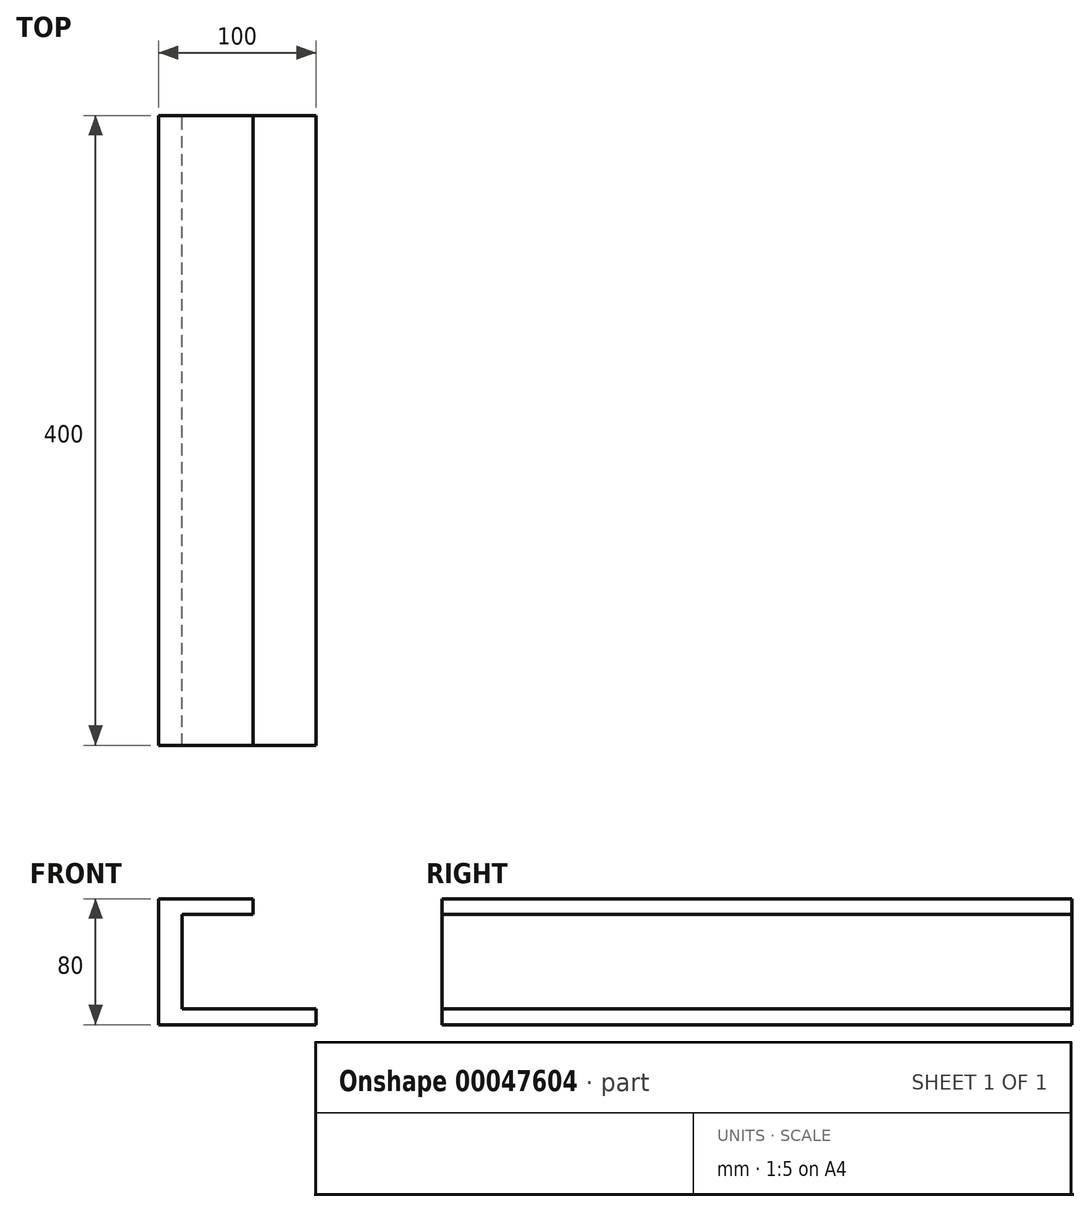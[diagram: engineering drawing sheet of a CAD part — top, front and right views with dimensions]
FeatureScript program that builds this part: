
annotation { "Feature Type Name" : "Feature", "Feature Type Description" : "" }
export const myFeature = defineFeature(function(context is Context, id is Id, definition is map)
    precondition{}
    {
        {
            var Q0;
            Q0=qCreatedBy(makeId("Front.planeOp"),FACE);
            var sketch = newSketch(context, id + "F0", { "sketchPlane" : qUnion([Q0])});
            skLineSegment(sketch, "E0.bottom", {"start": v(0, 0) * mm, "end": v(100, 0) * mm});
            skLineSegment(sketch, "E0.top", {"start": v(15, 10) * mm, "end": v(100, 10) * mm});
            skLineSegment(sketch, "E0.right", {"start": v(100, 0) * mm, "end": v(100, 10) * mm});
            skLineSegment(sketch, "E1", {"start": v(15, 10) * mm, "end": v(15, 70) * mm});
            skLineSegment(sketch, "E2", {"start": v(15, 70) * mm, "end": v(60, 70) * mm});
            skLineSegment(sketch, "E3", {"start": v(60, 70) * mm, "end": v(60, 80) * mm});
            skLineSegment(sketch, "E4", {"start": v(60, 80) * mm, "end": v(0, 80) * mm});
            skLineSegment(sketch, "E5", {"start": v(0, 80) * mm, "end": v(0, 0) * mm});
            skSolve(sketch);
        }
        {
            var Q0;
            Q0=makeQuery(id+"F0.imprint","IMPRINT",FACE,{"disambiguationData":[TD([[makeQuery(id+"F0.imprint","IMPRINT",EDGE,{"derivedFrom":sQuery(id+"F0.wireOp",EDGE,"E0.bottom")}),1.0]])]});
            extrude(context, id + "F1", {"entities" : qUnion([Q0]), "depth" : 400 * mm});
        }
    });
